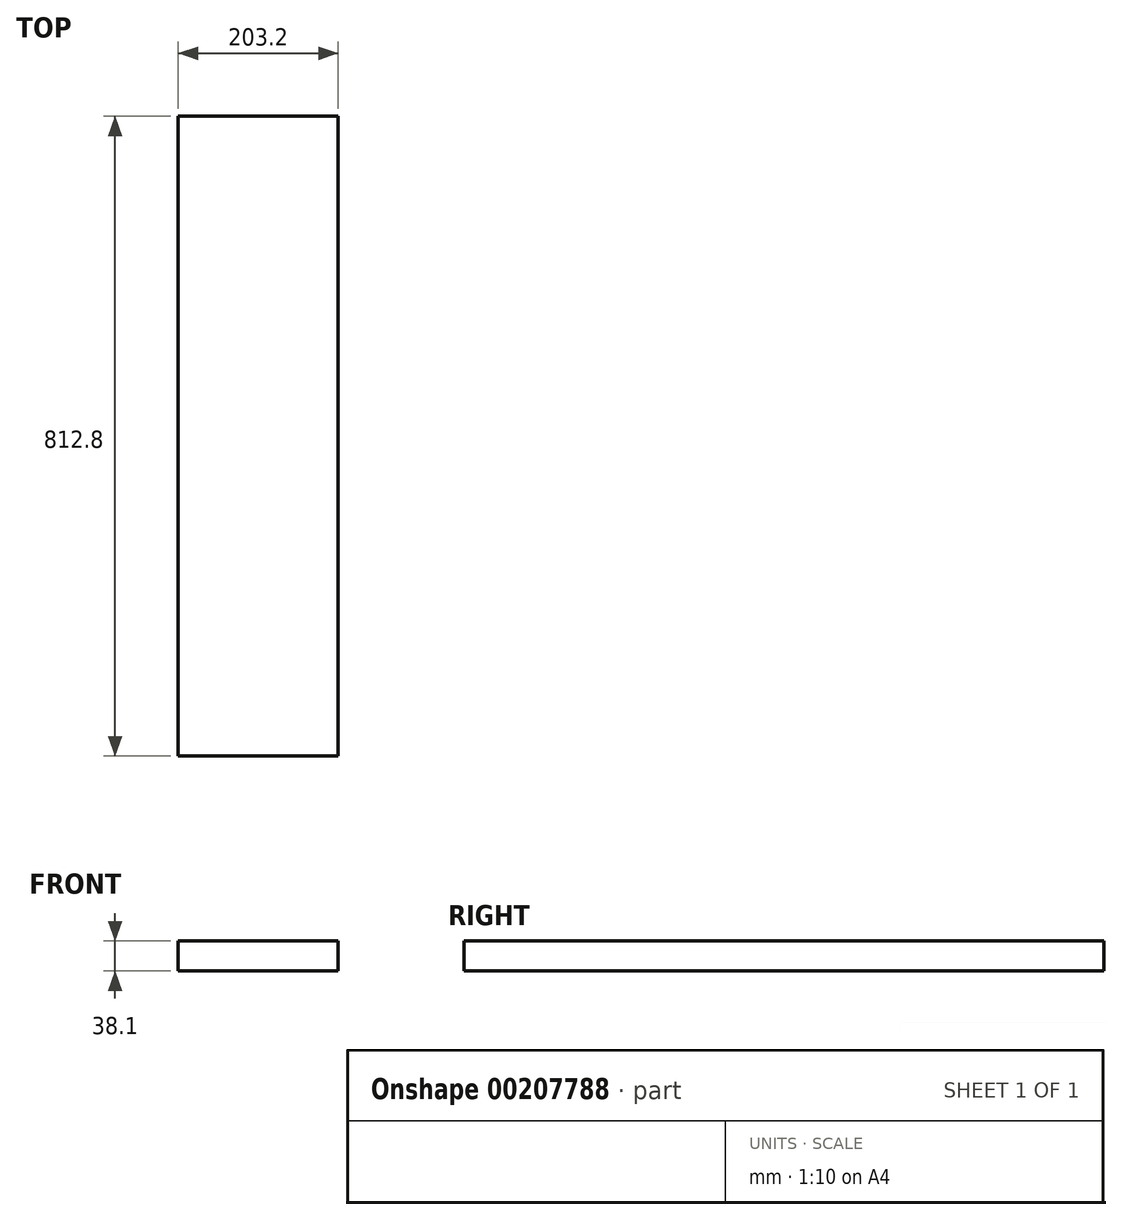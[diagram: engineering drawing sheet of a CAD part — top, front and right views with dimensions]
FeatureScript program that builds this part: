
annotation { "Feature Type Name" : "Feature", "Feature Type Description" : "" }
export const myFeature = defineFeature(function(context is Context, id is Id, definition is map)
    precondition{}
    {
        {
            var Q0;
            Q0=qCreatedBy(makeId("Front.planeOp"),FACE);
            var sketch = newSketch(context, id + "F0", { "sketchPlane" : qUnion([Q0])});
            skLineSegment(sketch, "E0.bottom", {"start": v(101.6, 19.05) * mm, "end": v(-101.6, 19.05) * mm});
            skLineSegment(sketch, "E0.top", {"start": v(101.6, -19.05) * mm, "end": v(-101.6, -19.05) * mm});
            skLineSegment(sketch, "E0.left", {"start": v(101.6, 19.05) * mm, "end": v(101.6, -19.05) * mm});
            skLineSegment(sketch, "E0.right", {"start": v(-101.6, 19.05) * mm, "end": v(-101.6, -19.05) * mm});
            skPoint(sketch, "E0.middle", {"position": v(0, 0) * mm});
            skSolve(sketch);
        }
        {
            var Q0;
            Q0 = qSketchRegion(id + "F0", true);
            extrude(context, id + "F1", {"entities" : qUnion([Q0]), "endBound" : BoundingType.SYMMETRIC, "depth" : 812.8 * mm});
        }
    });
